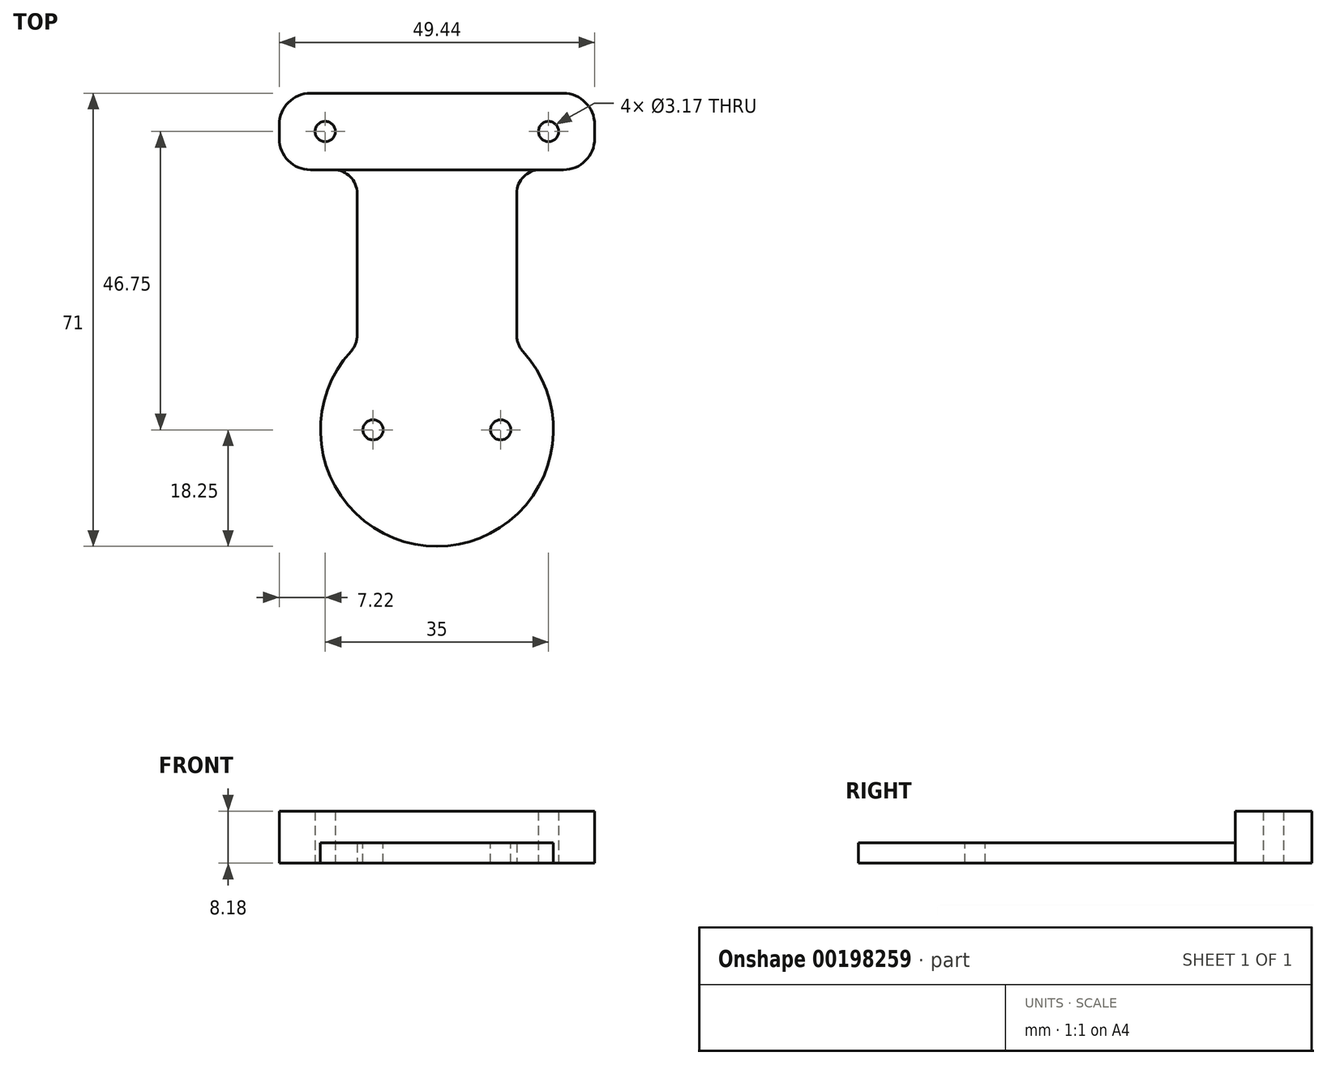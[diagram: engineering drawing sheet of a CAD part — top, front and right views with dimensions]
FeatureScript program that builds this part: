
annotation { "Feature Type Name" : "Feature", "Feature Type Description" : "" }
export const myFeature = defineFeature(function(context is Context, id is Id, definition is map)
    precondition{}
    {
        {
            var Q0;
            Q0=qCreatedBy(makeId("Top.planeOp"),FACE);
            var sketch = newSketch(context, id + "F0", { "sketchPlane" : qUnion([Q0])});
            skCircle(sketch, "E0", {"center": v(0, 0) * mm, "radius": 18.25 * mm});
            skLineSegment(sketch, "E1", {"start": v(-12.5, 13.3) * mm, "end": v(-12.5, 40.75) * mm});
            skLineSegment(sketch, "E2", {"start": v(-12.5, 40.75) * mm, "end": v(-24.72, 40.75) * mm});
            skLineSegment(sketch, "E3", {"start": v(-24.72, 40.75) * mm, "end": v(-24.72, 52.75) * mm});
            skLineSegment(sketch, "E4", {"start": v(-24.72, 52.75) * mm, "end": v(24.72, 52.75) * mm});
            skLineSegment(sketch, "E5", {"start": v(24.72, 52.75) * mm, "end": v(24.72, 40.75) * mm});
            skLineSegment(sketch, "E6", {"start": v(24.72, 40.75) * mm, "end": v(12.5, 40.75) * mm});
            skLineSegment(sketch, "E7", {"start": v(12.5, 40.75) * mm, "end": v(12.5, 13.3) * mm});
            skSolve(sketch);
        }
        {
            var Q0;
            {var subQ0=sQuery(id+"F0.wireOp",EDGE,"E1");Q0=makeQuery(id+"F0.imprint","IMPRINT",FACE,{"disambiguationData":[TD([[makeQuery(id+"F0.imprint","IMPRINT",EDGE,{"derivedFrom":subQ0}),-1.0]])]});}
            var Q1;
            {var subQ0=sQuery(id+"F0.wireOp",EDGE,"E0");var subQ1=makeQuery(id+"F0.imprint","INTERSECT",VERTEX,{"derivedFrom":[subQ0,sQuery(id+"F0.wireOp",EDGE,"E1")]});Q1=makeQuery(id+"F0.imprint","IMPRINT",FACE,{"disambiguationData":[TD([[makeQuery(id+"F0.imprint","IMPRINT",EDGE,{"disambiguationData":[TD([[subQ1,1.0]])],"derivedFrom":subQ0}),1.0]])]});}
            extrude(context, id + "F1", {"entities" : qUnion([Q0, Q1]), "depth" : 3.17 * mm});
        }
        {
            var Q0;
            Q0=makeQuery(id+"F1.opExtrude","CAP_FACE",FACE,{"disambiguationData":[OSD([sQuery(id+"F0.wireOp",EDGE,"E0"),sQuery(id+"F0.wireOp",EDGE,"E1"),sQuery(id+"F0.wireOp",EDGE,"E2"),sQuery(id+"F0.wireOp",EDGE,"E3"),sQuery(id+"F0.wireOp",EDGE,"E4"),sQuery(id+"F0.wireOp",EDGE,"E5"),sQuery(id+"F0.wireOp",EDGE,"E6"),sQuery(id+"F0.wireOp",EDGE,"E7")])],"isStart":false});
            var sketch = newSketch(context, id + "F2", { "sketchPlane" : qUnion([Q0])});
            skLineSegment(sketch, "E8", {"start": v(-12.5, 40.75) * mm, "end": v(12.5, 40.75) * mm});
            skSolve(sketch);
        }
        {
            var Q0;
            Q0=makeQuery(id+"F2.imprint","IMPRINT",FACE,{"disambiguationData":[TD([[makeQuery(id+"F2.imprint","IMPRINT",EDGE,{"derivedFrom":sQuery(id+"F2.wireOp",EDGE,"E8")}),1.0]])]});
            extrude(context, id + "F3", {"entities" : qUnion([Q0]), "operationType" : NewBodyOperationType.ADD, "depth" : 5 * mm});
        }
        {
            var Q0;
            Q0=makeQuery(id+"F1.opExtrude","SWEPT_EDGE",EDGE,{"disambiguationData":[OSD([sQuery(id+"F0.wireOp",EDGE,"E0"),sQuery(id+"F0.wireOp",EDGE,"E7")])]});
            var Q1;
            Q1=makeQuery(id+"F1.opExtrude","SWEPT_EDGE",EDGE,{"disambiguationData":[OSD([sQuery(id+"F0.wireOp",EDGE,"E0"),sQuery(id+"F0.wireOp",EDGE,"E1")])]});
            var Q2;
            Q2=makeQuery(id+"F1.opExtrude","SWEPT_EDGE",EDGE,{"disambiguationData":[OSD([sQuery(id+"F0.wireOp",EDGE,"E6"),sQuery(id+"F0.wireOp",EDGE,"E7")])]});
            var Q3;
            Q3=makeQuery(id+"F3.opExtrude","CAP_EDGE",EDGE,{"disambiguationData":[OSD([sQuery(id+"F0.wireOp",EDGE,"E2"),sQuery(id+"F0.wireOp",EDGE,"E6"),sQuery(id+"F2.wireOp",EDGE,"E8")])],"isStart":true});
            var Q4;
            Q4=makeQuery(id+"F1.opExtrude","SWEPT_EDGE",EDGE,{"disambiguationData":[OSD([sQuery(id+"F0.wireOp",EDGE,"E1"),sQuery(id+"F0.wireOp",EDGE,"E2")])]});
            fillet(context, id + "F4", {"entities" : qUnion([Q0, Q1, Q2, Q3, Q4]), "radius" : 3.68 * mm, "tangentPropagation" : true, "allowEdgeOverflow" : false});
        }
        {
            var Q0;
            Q0=makeQuery(id+"F1.opExtrude","CAP_FACE",FACE,{"disambiguationData":[OSD([sQuery(id+"F0.wireOp",EDGE,"E0"),sQuery(id+"F0.wireOp",EDGE,"E1"),sQuery(id+"F0.wireOp",EDGE,"E2"),sQuery(id+"F0.wireOp",EDGE,"E3"),sQuery(id+"F0.wireOp",EDGE,"E4"),sQuery(id+"F0.wireOp",EDGE,"E5"),sQuery(id+"F0.wireOp",EDGE,"E6"),sQuery(id+"F0.wireOp",EDGE,"E7")])],"isStart":false});
            var sketch = newSketch(context, id + "F5", { "sketchPlane" : qUnion([Q0])});
            skCircle(sketch, "E9", {"center": v(-10, 0) * mm, "radius": 1.59 * mm});
            skCircle(sketch, "E10", {"center": v(10, 0) * mm, "radius": 1.59 * mm});
            skCircle(sketch, "E11", {"center": v(17.5, 46.75) * mm, "radius": 1.59 * mm});
            skCircle(sketch, "E12", {"center": v(-17.5, 46.75) * mm, "radius": 1.59 * mm});
            skSolve(sketch);
        }
        {
            var Q0;
            Q0 = qSketchRegion(id + "F5", true);
            extrude(context, id + "F6", {"entities" : qUnion([Q0]), "operationType" : NewBodyOperationType.REMOVE, "depth" : 24.13 * mm});
        }
        {
            var Q0;
            Q0 = qSketchRegion(id + "F5", true);
            extrude(context, id + "F7", {"entities" : qUnion([Q0]), "operationType" : NewBodyOperationType.REMOVE, "oppositeDirection" : true, "depth" : 25.4 * mm});
        }
        {
            var Q0;
            {var subQ0=sQuery(id+"F0.wireOp",EDGE,"E6");var subQ1=sQuery(id+"F0.wireOp",EDGE,"E5");Q0=makeQuery(id+"F3.boolean.opBoolean","MERGE",EDGE,{"derivedFrom":[makeQuery(id+"F1.opExtrude","SWEPT_EDGE",EDGE,{"disambiguationData":[OSD([subQ1,subQ0])]}),makeQuery(id+"F3.opExtrude","SWEPT_EDGE",EDGE,{"disambiguationData":[OSD([subQ1,subQ0])]})]});}
            var Q1;
            {var subQ0=sQuery(id+"F0.wireOp",EDGE,"E5");var subQ1=sQuery(id+"F0.wireOp",EDGE,"E4");Q1=makeQuery(id+"F3.boolean.opBoolean","MERGE",EDGE,{"derivedFrom":[makeQuery(id+"F1.opExtrude","SWEPT_EDGE",EDGE,{"disambiguationData":[OSD([subQ1,subQ0])]}),makeQuery(id+"F3.opExtrude","SWEPT_EDGE",EDGE,{"disambiguationData":[OSD([subQ1,subQ0])]})]});}
            var Q2;
            {var subQ0=sQuery(id+"F0.wireOp",EDGE,"E4");var subQ1=sQuery(id+"F0.wireOp",EDGE,"E3");Q2=makeQuery(id+"F3.boolean.opBoolean","MERGE",EDGE,{"derivedFrom":[makeQuery(id+"F1.opExtrude","SWEPT_EDGE",EDGE,{"disambiguationData":[OSD([subQ1,subQ0])]}),makeQuery(id+"F3.opExtrude","SWEPT_EDGE",EDGE,{"disambiguationData":[OSD([subQ1,subQ0])]})]});}
            var Q3;
            {var subQ0=sQuery(id+"F0.wireOp",EDGE,"E3");var subQ1=sQuery(id+"F0.wireOp",EDGE,"E2");Q3=makeQuery(id+"F3.boolean.opBoolean","MERGE",EDGE,{"derivedFrom":[makeQuery(id+"F1.opExtrude","SWEPT_EDGE",EDGE,{"disambiguationData":[OSD([subQ1,subQ0])]}),makeQuery(id+"F3.opExtrude","SWEPT_EDGE",EDGE,{"disambiguationData":[OSD([subQ1,subQ0])]})]});}
            fillet(context, id + "F8", {"entities" : qUnion([Q0, Q1, Q2, Q3]), "radius" : 4.9 * mm, "tangentPropagation" : true, "allowEdgeOverflow" : false});
        }
    });
